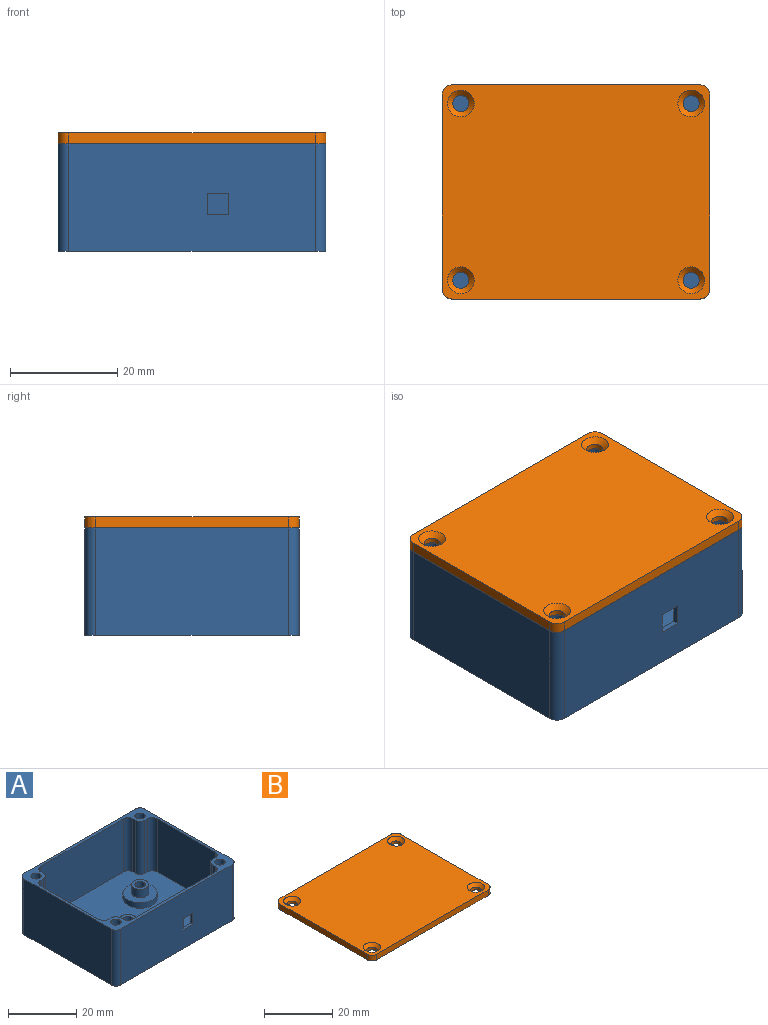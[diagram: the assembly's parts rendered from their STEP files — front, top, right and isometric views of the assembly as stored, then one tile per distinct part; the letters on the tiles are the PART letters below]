
ASSEMBLY  parts=2 mates=1
PART A: 71 faces, bbox 50x40x20 mm
  f0: plane 34x19mm, normal (0,1,0), area 630mm2, adj f5,f9,f58,f62,f67,f68,f69,f70
  f1: plane 46x20mm, normal (0,-1,0), area 904mm2, adj f2,f9,f52,f53,f67,f68,f69,f70
  f2: plane 50x40mm, normal (0,0,-1), area 1949.8mm2, adj f1,f10,f11,f12,f37,f38,f39,f40
  f3: cylinder r=1.5mm len=4mm, axis (0,0,-1), area 37.7mm2, adj f30,f50
  f4: cylinder r=1.5mm len=4mm, axis (0,0,-1), area 37.7mm2, adj f32,f43
  f5: plane 48x38mm, normal (0,0,1), area 1563.5mm2, adj f0,f6,f7,f8,f13,f14,f15,f16
  f6: plane 24x19mm, normal (-1,0,0), area 456mm2, adj f5,f9,f57,f60
  f7: plane 34x19mm, normal (0,-1,0), area 646mm2, adj f5,f9,f56,f64
  f8: plane 24x19mm, normal (1,0,0), area 456mm2, adj f5,f9,f61,f66
  f9: plane 50x40mm, normal (0,0,1), area 247.7mm2, adj f0,f1,f6,f7,f8,f10,f11,f12
  f10: plane 46x20mm, normal (0,1,0), area 920mm2, adj f2,f9,f51,f54
  f11: plane 36x20mm, normal (-1,0,0), area 720mm2, adj f2,f9,f51,f52
  f12: plane 36x20mm, normal (1,0,0), area 720mm2, adj f2,f9,f53,f54
  f13: plane 19x1mm, normal (0,-1,0), area 19mm2, adj f5,f9,f65,f66
  f14: plane 19x1mm, normal (1,0,0), area 19mm2, adj f5,f9,f64,f65
  f15: plane 19x1mm, normal (0,-1,0), area 19mm2, adj f5,f9,f55,f57
  f16: plane 19x1mm, normal (-1,0,0), area 19mm2, adj f5,f9,f55,f56
  f17: plane 19x1mm, normal (0,1,0), area 19mm2, adj f5,f9,f61,f63
  f18: plane 19x1mm, normal (1,0,0), area 19mm2, adj f5,f9,f62,f63
  f19: plane 19x1mm, normal (0,1,0), area 19mm2, adj f5,f9,f59,f60
  f20: plane 19x1mm, normal (-1,0,0), area 19mm2, adj f5,f9,f58,f59
  f21: cylinder r=1.5mm len=10mm, axis (0,0,1), area 94.2mm2, adj f9,f22
  f22: plane 3x3mm, normal (0,0,1), area 7.1mm2, adj f21
  f23: cylinder r=1.5mm len=10mm, axis (0,0,1), area 94.2mm2, adj f9,f24
  f24: plane 3x3mm, normal (0,0,1), area 7.1mm2, adj f23
  f25: cylinder r=1.5mm len=10mm, axis (0,0,1), area 94.2mm2, adj f9,f26
  f26: plane 3x3mm, normal (0,0,1), area 7.1mm2, adj f25
  f27: cylinder r=1.5mm len=10mm, axis (0,0,1), area 94.2mm2, adj f9,f28
  f28: plane 3x3mm, normal (0,0,1), area 7.1mm2, adj f27
  f29: cylinder r=2.5mm len=5mm, axis (0,0,-1), area 47.1mm2, adj f30,f34
  f30: plane 5x5mm, normal (0,0,1), area 12.6mm2, adj f3,f29
  f31: cylinder r=2.5mm len=5mm, axis (0,0,-1), area 47.1mm2, adj f32,f36
  f32: plane 5x5mm, normal (0,0,1), area 12.6mm2, adj f4,f31
  f33: cylinder r=5mm len=10mm, axis (0,0,-1), area 62.8mm2, adj f5,f34
  f34: plane 10x10mm, normal (0,0,1), area 58.9mm2, adj f29,f33
  f35: cylinder r=5mm len=10mm, axis (0,0,-1), area 62.8mm2, adj f5,f36
  f36: plane 10x10mm, normal (0,0,1), area 58.9mm2, adj f31,f35
  f37: plane 2.6x2mm, normal (0.5,0.87,0), area 6mm2, adj f2,f38,f42,f43
  f38: plane 3x2mm, normal (1,0,0), area 6mm2, adj f2,f37,f39,f43
  f39: plane 2.6x2mm, normal (0.5,-0.87,0), area 6mm2, adj f2,f38,f40,f43
  f40: plane 2.6x2mm, normal (-0.5,-0.87,0), area 6mm2, adj f2,f39,f41,f43
  f41: plane 3x2mm, normal (-1,0,0), area 6mm2, adj f2,f40,f42,f43
  f42: plane 2.6x2mm, normal (-0.5,0.87,0), area 6mm2, adj f2,f37,f41,f43
  f43: plane 6x5.2mm, normal (0,0,-1), area 16.3mm2, adj f4,f37,f38,f39,f40,f41,f42
  f44: plane 2.6x2mm, normal (0.5,0.87,0), area 6mm2, adj f2,f45,f49,f50
  f45: plane 3x2mm, normal (1,0,0), area 6mm2, adj f2,f44,f46,f50
  f46: plane 2.6x2mm, normal (0.5,-0.87,0), area 6mm2, adj f2,f45,f47,f50
  f47: plane 2.6x2mm, normal (-0.5,-0.87,0), area 6mm2, adj f2,f46,f48,f50
  f48: plane 3x2mm, normal (-1,0,0), area 6mm2, adj f2,f47,f49,f50
  f49: plane 2.6x2mm, normal (-0.5,0.87,0), area 6mm2, adj f2,f44,f48,f50
  f50: plane 6x5.2mm, normal (0,0,-1), area 16.3mm2, adj f3,f44,f45,f46,f47,f48,f49
  f51: cylinder r=2mm len=20mm, axis (0,0,1), area 62.8mm2, adj f2,f9,f10,f11
  f52: cylinder r=2mm len=20mm, axis (0,0,-1), area 62.8mm2, adj f1,f2,f9,f11
  f53: cylinder r=2mm len=20mm, axis (0,0,1), area 62.8mm2, adj f1,f2,f9,f12
  f54: cylinder r=2mm len=20mm, axis (0,0,-1), area 62.8mm2, adj f2,f9,f10,f12
  f55: cylinder r=2mm len=19mm, axis (0,0,1), area 59.7mm2, adj f5,f9,f15,f16
  f56: cylinder r=2mm len=19mm, axis (0,0,1), area 59.7mm2, adj f5,f7,f9,f16
  f57: cylinder r=2mm len=19mm, axis (0,0,1), area 59.7mm2, adj f5,f6,f9,f15
  f58: cylinder r=2mm len=19mm, axis (0,0,1), area 59.7mm2, adj f0,f5,f9,f20
  f59: cylinder r=2mm len=19mm, axis (0,0,1), area 59.7mm2, adj f5,f9,f19,f20
  f60: cylinder r=2mm len=19mm, axis (0,0,-1), area 59.7mm2, adj f5,f6,f9,f19
  f61: cylinder r=2mm len=19mm, axis (0,0,-1), area 59.7mm2, adj f5,f8,f9,f17
  f62: cylinder r=2mm len=19mm, axis (0,0,-1), area 59.7mm2, adj f0,f5,f9,f18
  f63: cylinder r=2mm len=19mm, axis (0,0,1), area 59.7mm2, adj f5,f9,f17,f18
  f64: cylinder r=2mm len=19mm, axis (0,0,-1), area 59.7mm2, adj f5,f7,f9,f14
  f65: cylinder r=2mm len=19mm, axis (0,0,1), area 59.7mm2, adj f5,f9,f13,f14
  f66: cylinder r=2mm len=19mm, axis (0,0,1), area 59.7mm2, adj f5,f8,f9,f13
  f67: plane 4x1mm, normal (0,0,-1), area 4mm2, adj f0,f1,f68,f70
  f68: plane 4x1mm, normal (1,0,0), area 4mm2, adj f0,f1,f67,f69
  f69: plane 4x1mm, normal (0,0,1), area 4mm2, adj f0,f1,f68,f70
  f70: plane 4x1mm, normal (-1,0,0), area 4mm2, adj f0,f1,f67,f69
PART B: 18 faces, bbox 50x40x2 mm
  f0: plane 46x2mm, normal (0,1,0), area 92mm2, adj f4,f5,f14,f17
  f1: plane 36x2mm, normal (-1,0,0), area 72mm2, adj f4,f5,f14,f15
  f2: plane 46x2mm, normal (0,-1,0), area 92mm2, adj f4,f5,f15,f16
  f3: plane 36x2mm, normal (1,0,0), area 72mm2, adj f4,f5,f16,f17
  f4: plane 50x40mm, normal (0,0,1), area 1918mm2, adj f0,f1,f2,f3,f10,f11,f12,f13
  f5: plane 50x40mm, normal (0,0,-1), area 1968.3mm2, adj f0,f1,f2,f3,f6,f7,f8,f9
  f6: cylinder r=1.5mm len=3mm, axis (0,0,1), area 9.4mm2, adj f5,f13
  f7: cylinder r=1.5mm len=3mm, axis (0,0,1), area 9.4mm2, adj f5,f10
  f8: cylinder r=1.5mm len=3mm, axis (0,0,1), area 9.4mm2, adj f5,f11
  f9: cylinder r=1.5mm len=3mm, axis (0,0,1), area 9.4mm2, adj f5,f12
  f10: cone r=1.5mm half-angle=45deg, axis (0,0,1), area 17.8mm2, adj f4,f7
  f11: cone r=1.5mm half-angle=45deg, axis (0,0,1), area 17.8mm2, adj f4,f8
  f12: cone r=1.5mm half-angle=45deg, axis (0,0,1), area 17.8mm2, adj f4,f9
  f13: cone r=1.5mm half-angle=45deg, axis (0,0,1), area 17.8mm2, adj f4,f6
  f14: cylinder r=2mm len=2mm, axis (0,0,1), area 6.3mm2, adj f0,f1,f4,f5
  f15: cylinder r=2mm len=2mm, axis (0,0,-1), area 6.3mm2, adj f1,f2,f4,f5
  f16: cylinder r=2mm len=2mm, axis (0,0,1), area 6.3mm2, adj f2,f3,f4,f5
  f17: cylinder r=2mm len=2mm, axis (0,0,-1), area 6.3mm2, adj f0,f3,f4,f5
PLACE A t=(29.64,-36.04,-26.89)mm
PLACE B t=(-39.33,-35.91,-6.81)mm
MATE slider A.f25 <-> B.f8  axis (0,0,1) through (17.39,-25.45,-6.89)mm
